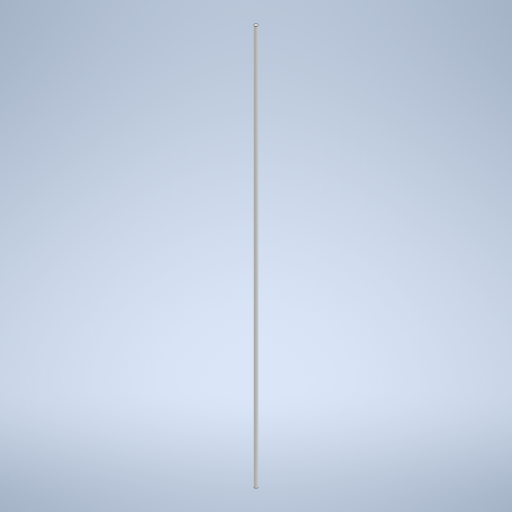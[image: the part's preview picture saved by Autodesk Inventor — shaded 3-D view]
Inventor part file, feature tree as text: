
AUTODESK INVENTOR PART (.ipt)
format: ipt  version: 2023 (Build 270158030, 158C)  size: 231,936 bytes
history: native  units: in
note: dims shown in document units (in); Inventor stores cm internally (conversion verified against a paired STEP export)
features: extrude x1, sketch x1
ambient origin geometry x8: Origin, YZ Plane, XZ Plane, XY Plane, X Axis, Y Axis, Z Axis, Center Point
bodies: Solid1 (feature_tree)
feature tree (2):
  extrude  "Extrusion1"  Depth=30.125in TaperAngle=0.0deg
  sketch  "Sketch1"  dims[d0=0.25in d1=30.125in d2=0.0in]
